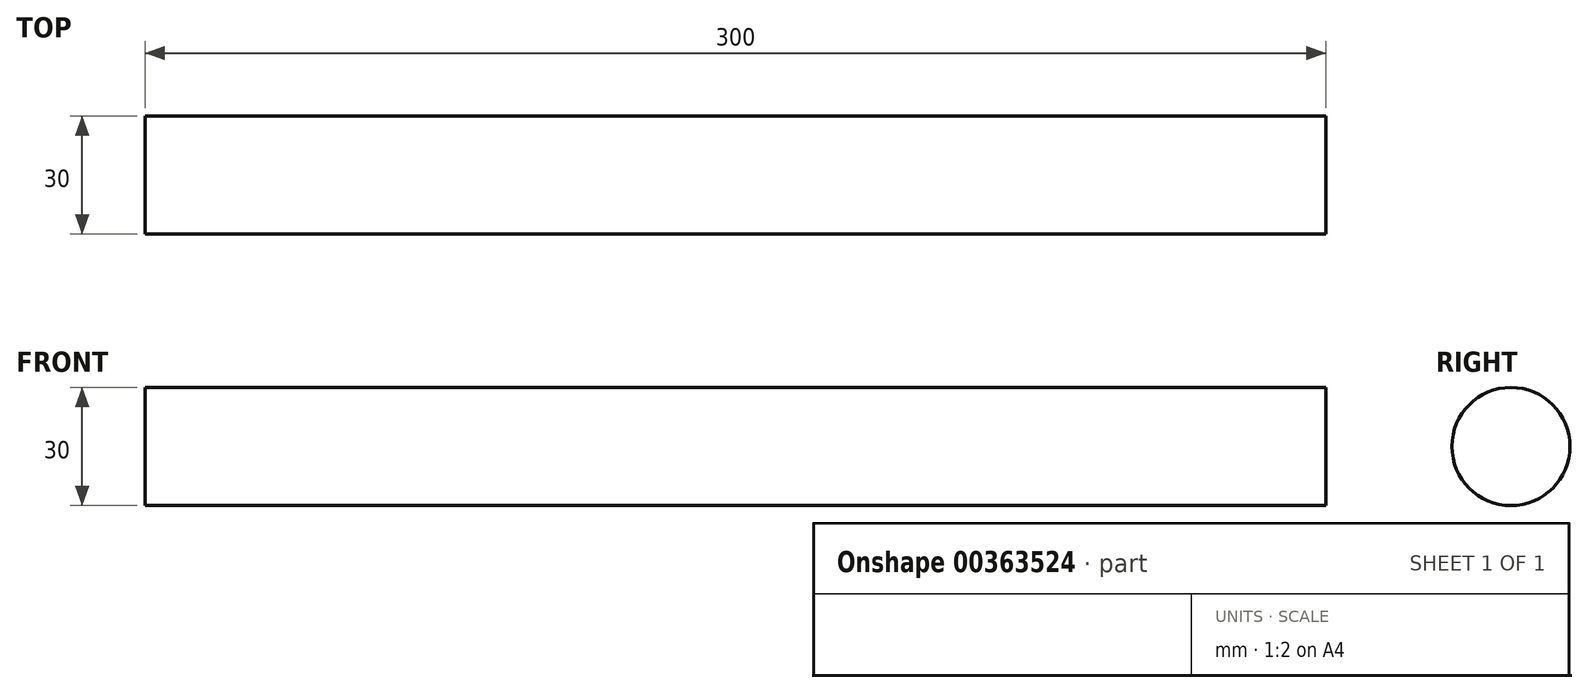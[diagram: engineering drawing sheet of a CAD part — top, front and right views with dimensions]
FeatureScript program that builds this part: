
annotation { "Feature Type Name" : "Feature", "Feature Type Description" : "" }
export const myFeature = defineFeature(function(context is Context, id is Id, definition is map)
    precondition{}
    {
        {
            var Q0;
            Q0=qCreatedBy(makeId("Right.planeOp"),FACE);
            var sketch = newSketch(context, id + "F0", { "sketchPlane" : qUnion([Q0])});
            skCircle(sketch, "E0", {"center": v(0, 0) * mm, "radius": 15 * mm});
            skSolve(sketch);
        }
        {
            var Q0;
            Q0=makeQuery(id+"F0.imprint","IMPRINT",FACE,{"disambiguationData":[TD([[makeQuery(id+"F0.imprint","IMPRINT",EDGE,{"derivedFrom":sQuery(id+"F0.wireOp",EDGE,"E0")}),1.0]])]});
            extrude(context, id + "F1", {"entities" : qUnion([Q0]), "endBound" : BoundingType.SYMMETRIC, "depth" : 300 * mm});
        }
    });
